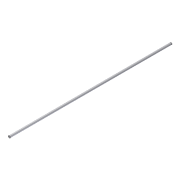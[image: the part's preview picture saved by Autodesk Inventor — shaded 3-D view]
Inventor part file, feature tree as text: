
AUTODESK INVENTOR PART (.ipt)
format: ipt  version: 2012 (Build 160160000, 160)  size: 60,416 bytes
history: native  units: in
note: dims shown in document units (in); Inventor stores cm internally (conversion verified against a paired STEP export)
features: extrude x1, plane x1, sketch x1, other x1
ambient origin geometry x8: Origin, YZ Plane, XZ Plane, XY Plane, X Axis, Y Axis, Z Axis, Center Point
bodies: Solid1 (feature_tree)
feature tree (4):
  extrude  "Extrusion1"  Depth=19.0in TaperAngle=0.0deg
  plane  "Work Plane1"
  sketch  "Sketch1"  dims[d0=0.25in d1=19.0in d2=0.0in d3=90.0deg]
  other  "Work Axis1"
